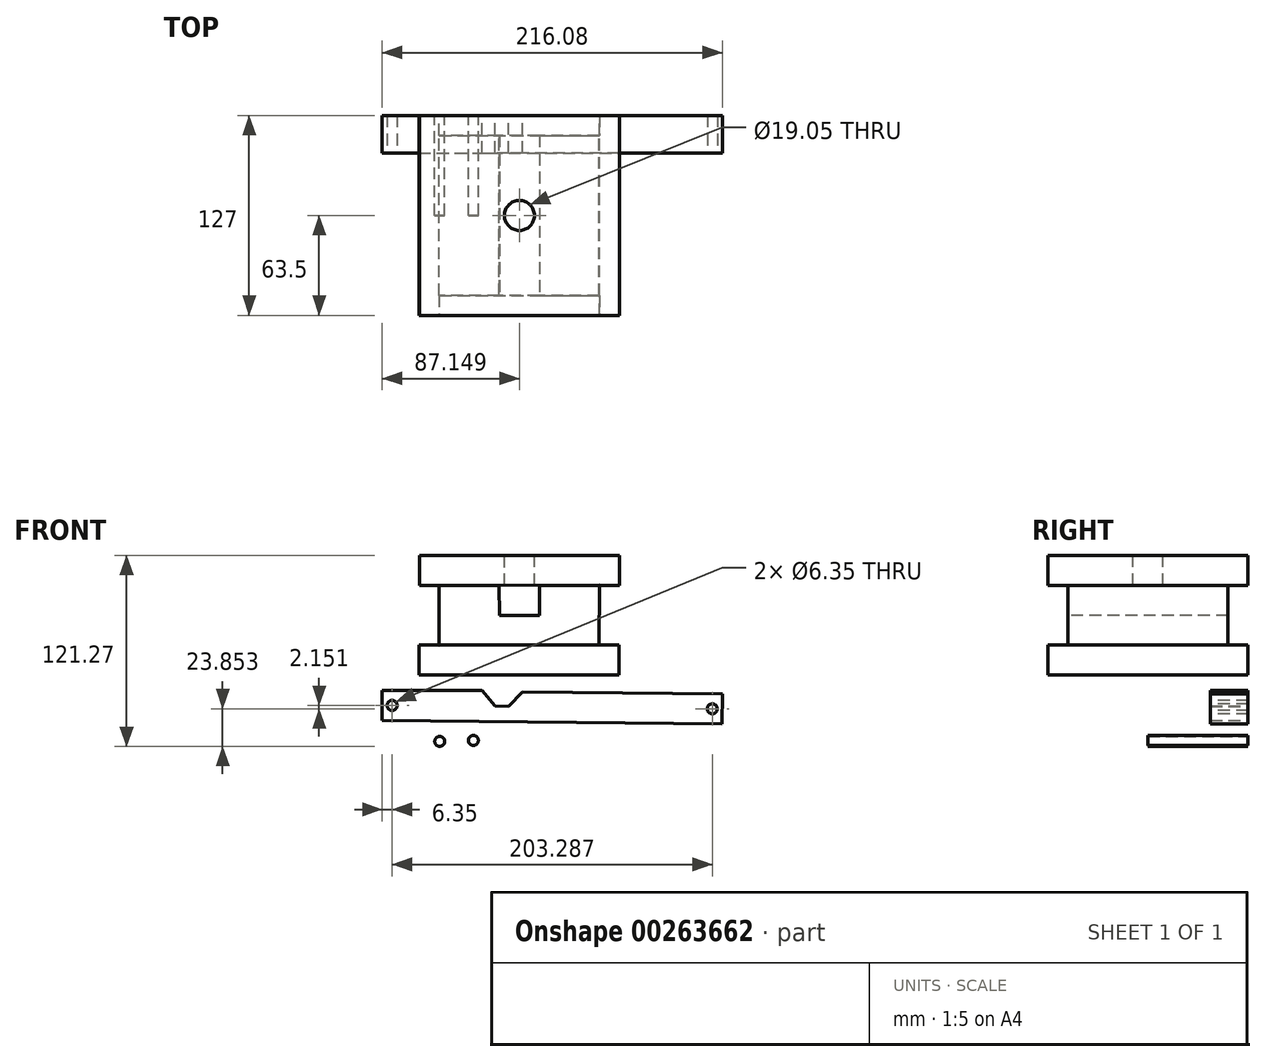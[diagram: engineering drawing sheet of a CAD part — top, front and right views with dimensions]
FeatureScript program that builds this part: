
annotation { "Feature Type Name" : "Feature", "Feature Type Description" : "" }
export const myFeature = defineFeature(function(context is Context, id is Id, definition is map)
    precondition{}
    {
        {
            var Q0;
            Q0=qCreatedBy(makeId("Front.planeOp"),FACE);
            var sketch = newSketch(context, id + "F0", { "sketchPlane" : qUnion([Q0])});
            skLineSegment(sketch, "E0", {"start": v(-76.14, 56.97) * mm, "end": v(50.86, 56.97) * mm});
            skLineSegment(sketch, "E1", {"start": v(50.86, 56.97) * mm, "end": v(50.86, 37.92) * mm});
            skLineSegment(sketch, "E2", {"start": v(-76.14, 56.97) * mm, "end": v(-76.14, 37.92) * mm});
            skLineSegment(sketch, "E3", {"start": v(-76.14, 37.92) * mm, "end": v(50.86, 37.92) * mm});
            skSolve(sketch);
        }
        {
            var Q0;
            Q0=qCreatedBy(makeId("Front.planeOp"),FACE);
            var sketch = newSketch(context, id + "F1", { "sketchPlane" : qUnion([Q0])});
            skLineSegment(sketch, "E4", {"start": v(38.12, 38.1) * mm, "end": v(-63.6, 37.91) * mm});
            skLineSegment(sketch, "E5", {"start": v(-63.6, 37.91) * mm, "end": v(-63.53, -0.18) * mm});
            skLineSegment(sketch, "E6", {"start": v(-63.53, -0.18) * mm, "end": v(38.07, 0) * mm});
            skLineSegment(sketch, "E7", {"start": v(38.07, 0) * mm, "end": v(38.12, 38.1) * mm});
            skSolve(sketch);
        }
        {
            var Q0;
            Q0=qCreatedBy(makeId("Front.planeOp"),FACE);
            var sketch = newSketch(context, id + "F2", { "sketchPlane" : qUnion([Q0])});
            skLineSegment(sketch, "E8", {"start": v(-76.45, 0) * mm, "end": v(50.55, 0) * mm});
            skLineSegment(sketch, "E9", {"start": v(50.55, 0) * mm, "end": v(50.55, -19.05) * mm});
            skLineSegment(sketch, "E10", {"start": v(-76.45, 0) * mm, "end": v(-76.45, -19.05) * mm});
            skLineSegment(sketch, "E11", {"start": v(-76.45, -19.05) * mm, "end": v(50.55, -19.05) * mm});
            skSolve(sketch);
        }
        {
            var Q0;
            Q0=makeQuery(id+"F0.imprint","IMPRINT",FACE,{"disambiguationData":[TD([[makeQuery(id+"F0.imprint","IMPRINT",EDGE,{"derivedFrom":sQuery(id+"F0.wireOp",EDGE,"E0")}),-1.0]])]});
            extrude(context, id + "F3", {"entities" : qUnion([Q0]), "depth" : 127 * mm});
        }
        {
            var Q0;
            Q0=makeQuery(id+"F2.imprint","IMPRINT",FACE,{"disambiguationData":[TD([[makeQuery(id+"F2.imprint","IMPRINT",EDGE,{"derivedFrom":sQuery(id+"F2.wireOp",EDGE,"E8")}),-1.0]])]});
            extrude(context, id + "F4", {"entities" : qUnion([Q0]), "depth" : 127 * mm});
        }
        {
            var Q0;
            Q0=makeQuery(id+"F1.imprint","IMPRINT",FACE,{"disambiguationData":[TD([[makeQuery(id+"F1.imprint","IMPRINT",EDGE,{"derivedFrom":sQuery(id+"F1.wireOp",EDGE,"E4")}),1.0]])]});
            extrude(context, id + "F5", {"entities" : qUnion([Q0]), "depth" : 127 * mm});
        }
        {
            var Q0;
            Q0=makeQuery(id+"F5.opExtrude","CAP_FACE",FACE,{"disambiguationData":[OSD([sQuery(id+"F1.wireOp",EDGE,"E4"),sQuery(id+"F1.wireOp",EDGE,"E5"),sQuery(id+"F1.wireOp",EDGE,"E6"),sQuery(id+"F1.wireOp",EDGE,"E7")])],"isStart":true});
            extrude(context, id + "F6", {"entities" : qUnion([Q0]), "operationType" : NewBodyOperationType.REMOVE, "oppositeDirection" : true, "depth" : 12.7 * mm});
        }
        {
            var Q0;
            Q0=makeQuery(id+"F5.opExtrude","CAP_FACE",FACE,{"disambiguationData":[OSD([sQuery(id+"F1.wireOp",EDGE,"E4"),sQuery(id+"F1.wireOp",EDGE,"E5"),sQuery(id+"F1.wireOp",EDGE,"E6"),sQuery(id+"F1.wireOp",EDGE,"E7")])],"isStart":false});
            extrude(context, id + "F7", {"entities" : qUnion([Q0]), "operationType" : NewBodyOperationType.REMOVE, "oppositeDirection" : true, "depth" : 12.7 * mm});
        }
        {
            var Q0;
            {var subQ0=sQuery(id+"F1.wireOp",EDGE,"E4");var subQ1=sQuery(id+"F1.wireOp",EDGE,"E6");var subQ2=sQuery(id+"F1.wireOp",EDGE,"E7");var subQ3=sQuery(id+"F1.wireOp",EDGE,"E5");Q0=makeQuery(id+"F7.boolean.opBoolean","COPY",FACE,{"disambiguationData":[TD([makeQuery(id+"F5.opExtrude","SWEPT_FACE",FACE,{"disambiguationData":[OSD([subQ0])]})])],"derivedFrom":makeQuery(id+"F7.opExtrude","CAP_FACE",FACE,{"disambiguationData":[OSD([subQ0,subQ3,subQ1,subQ2])],"isStart":false})});}
            var sketch = newSketch(context, id + "F8", { "sketchPlane" : qUnion([Q0])});
            skLineSegment(sketch, "E12", {"start": v(-63.6, 37.91) * mm, "end": v(-25.5, 37.98) * mm});
            skLineSegment(sketch, "E13", {"start": v(38.12, 38.1) * mm, "end": v(0, 38.03) * mm});
            skLineSegment(sketch, "E14", {"start": v(0, 38.03) * mm, "end": v(0.03, 18.98) * mm});
            skLineSegment(sketch, "E15", {"start": v(0.03, 18.98) * mm, "end": v(-25.37, 18.93) * mm});
            skLineSegment(sketch, "E16", {"start": v(-25.37, 18.93) * mm, "end": v(-25.5, 37.98) * mm});
            skLineSegment(sketch, "E17", {"start": v(-25.5, 37.98) * mm, "end": v(0, 38.03) * mm});
            skSolve(sketch);
        }
        {
            var Q0;
            Q0=makeQuery(id+"F8.imprint","IMPRINT",FACE,{"disambiguationData":[TD([[makeQuery(id+"F8.imprint","IMPRINT",EDGE,{"derivedFrom":sQuery(id+"F8.wireOp",EDGE,"E14")}),-1.0]])]});
            extrude(context, id + "F9", {"entities" : qUnion([Q0]), "operationType" : NewBodyOperationType.REMOVE, "endBound" : BoundingType.THROUGH_ALL, "oppositeDirection" : true, "depth" : 25.4 * mm});
        }
        {
            var Q0;
            Q0=makeQuery(id+"F3.opExtrude","SWEPT_FACE",FACE,{"disambiguationData":[OSD([sQuery(id+"F0.wireOp",EDGE,"E0")])]});
            var sketch = newSketch(context, id + "F10", { "sketchPlane" : qUnion([Q0])});
            skLineSegment(sketch, "E18", {"start": v(-12.64, 0) * mm, "end": v(-12.64, -63.5) * mm});
            skPoint(sketch, "E18.endSnap0", {"position": v(-12.64, -127) * mm});
            skSolve(sketch);
        }
        {
            var Q0;
            Q0=sQuery(id+"F10.wireOp",VERTEX,"E18.end");
            var Q1;
            Q1=makeQuery(id+"F3.opExtrude","SWEPT_BODY",BODY,{"disambiguationData":[OSD([sQuery(id+"F0.wireOp",EDGE,"E0"),sQuery(id+"F0.wireOp",EDGE,"E1"),sQuery(id+"F0.wireOp",EDGE,"E2"),sQuery(id+"F0.wireOp",EDGE,"E3")])]});
            var Q2;
            Q2=makeQuery(id+"F4.opExtrude","SWEPT_BODY",BODY,{"disambiguationData":[OSD([sQuery(id+"F2.wireOp",EDGE,"E8"),sQuery(id+"F2.wireOp",EDGE,"E9"),sQuery(id+"F2.wireOp",EDGE,"E10"),sQuery(id+"F2.wireOp",EDGE,"E11")])]});
            var Q3;
            Q3=makeQuery(id+"F5.opExtrude","SWEPT_BODY",BODY,{"disambiguationData":[OSD([sQuery(id+"F1.wireOp",EDGE,"E4"),sQuery(id+"F1.wireOp",EDGE,"E5"),sQuery(id+"F1.wireOp",EDGE,"E6"),sQuery(id+"F1.wireOp",EDGE,"E7")])]});
            hole(context, id + "F11", {"style" : HoleStyle.SIMPLE, "endStyle" : HoleEndStyle.BLIND, "holeDiameter" : 19.05 * mm, "holeDepth" : 19.05 * mm, "tappedDepth" : 12.7 * mm, "tapClearance" : 3, "locations" : qUnion([Q0]), "scope" : qUnion([Q1, Q2, Q3])});
        }
        {
            var Q0;
            Q0=qCreatedBy(makeId("Front.planeOp"),FACE);
            var sketch = newSketch(context, id + "F12", { "sketchPlane" : qUnion([Q0])});
            skLineSegment(sketch, "E19", {"start": v(-99.79, -47.82) * mm, "end": v(116.1, -50.04) * mm});
            skLineSegment(sketch, "E20", {"start": v(116.1, -50.04) * mm, "end": v(116.3, -30.99) * mm});
            skLineSegment(sketch, "E21", {"start": v(-99.79, -47.82) * mm, "end": v(-99.79, -28.77) * mm});
            skLineSegment(sketch, "E22", {"start": v(-99.79, -28.77) * mm, "end": v(-36.29, -28.77) * mm});
            skLineSegment(sketch, "E23", {"start": v(116.3, -30.99) * mm, "end": v(-10.7, -29.68) * mm});
            skLineSegment(sketch, "E24", {"start": v(-36.29, -28.77) * mm, "end": v(-28.15, -38.52) * mm});
            skLineSegment(sketch, "E25", {"start": v(-10.7, -29.68) * mm, "end": v(-19.4, -38.93) * mm});
            skLineSegment(sketch, "E26", {"start": v(-19.4, -38.93) * mm, "end": v(-28.15, -38.52) * mm});
            skSolve(sketch);
        }
        {
            var Q0;
            Q0=makeQuery(id+"F12.imprint","IMPRINT",FACE,{"disambiguationData":[TD([[makeQuery(id+"F12.imprint","IMPRINT",EDGE,{"derivedFrom":sQuery(id+"F12.wireOp",EDGE,"E19")}),1.0]])]});
            extrude(context, id + "F13", {"entities" : qUnion([Q0]), "depth" : 23.83 * mm});
        }
        {
            var Q0;
            Q0=makeQuery(id+"F13.opExtrude","CAP_FACE",FACE,{"disambiguationData":[OSD([sQuery(id+"F12.wireOp",EDGE,"E19"),sQuery(id+"F12.wireOp",EDGE,"E20"),sQuery(id+"F12.wireOp",EDGE,"E21"),sQuery(id+"F12.wireOp",EDGE,"E22"),sQuery(id+"F12.wireOp",EDGE,"E23"),sQuery(id+"F12.wireOp",EDGE,"E24"),sQuery(id+"F12.wireOp",EDGE,"E25"),sQuery(id+"F12.wireOp",EDGE,"E26")])],"isStart":false});
            var sketch = newSketch(context, id + "F14", { "sketchPlane" : qUnion([Q0])});
            skLineSegment(sketch, "E27", {"start": v(-99.79, -38.3) * mm, "end": v(-93.44, -38.3) * mm});
            skLineSegment(sketch, "E28", {"start": v(116.2, -40.51) * mm, "end": v(109.85, -40.45) * mm});
            skSolve(sketch);
        }
        {
            var Q0;
            Q0=sQuery(id+"F14.wireOp",VERTEX,"E27.end");
            var Q1;
            Q1=sQuery(id+"F14.wireOp",VERTEX,"E28.end");
            var Q2;
            Q2=makeQuery(id+"F13.opExtrude","SWEPT_BODY",BODY,{"disambiguationData":[OSD([sQuery(id+"F12.wireOp",EDGE,"E19"),sQuery(id+"F12.wireOp",EDGE,"E20"),sQuery(id+"F12.wireOp",EDGE,"E21"),sQuery(id+"F12.wireOp",EDGE,"E22"),sQuery(id+"F12.wireOp",EDGE,"E23"),sQuery(id+"F12.wireOp",EDGE,"E24"),sQuery(id+"F12.wireOp",EDGE,"E25"),sQuery(id+"F12.wireOp",EDGE,"E26")])]});
            hole(context, id + "F15", {"style" : HoleStyle.SIMPLE, "endStyle" : HoleEndStyle.THROUGH, "holeDiameter" : 6.35 * mm, "tappedDepth" : 12.7 * mm, "tapClearance" : 3, "locations" : qUnion([Q0, Q1]), "scope" : qUnion([Q2])});
        }
        {
            var Q0;
            Q0=qCreatedBy(makeId("Front.planeOp"),FACE);
            var sketch = newSketch(context, id + "F16", { "sketchPlane" : qUnion([Q0])});
            skCircle(sketch, "E29", {"center": v(-63.25, -61.13) * mm, "radius": 3.18 * mm});
            skCircle(sketch, "E30", {"center": v(-41.89, -60.51) * mm, "radius": 3.18 * mm});
            skSolve(sketch);
        }
        {
            var Q0;
            Q0=makeQuery(id+"F16.imprint","IMPRINT",FACE,{"disambiguationData":[TD([[makeQuery(id+"F16.imprint","IMPRINT",EDGE,{"derivedFrom":sQuery(id+"F16.wireOp",EDGE,"E29")}),1.0]])]});
            extrude(context, id + "F17", {"entities" : qUnion([Q0]), "depth" : 63.5 * mm});
        }
        {
            var Q0;
            Q0 = qSketchRegion(id + "F16", true);
            extrude(context, id + "F18", {"entities" : qUnion([Q0]), "operationType" : NewBodyOperationType.ADD, "depth" : 63.5 * mm});
        }
    });
